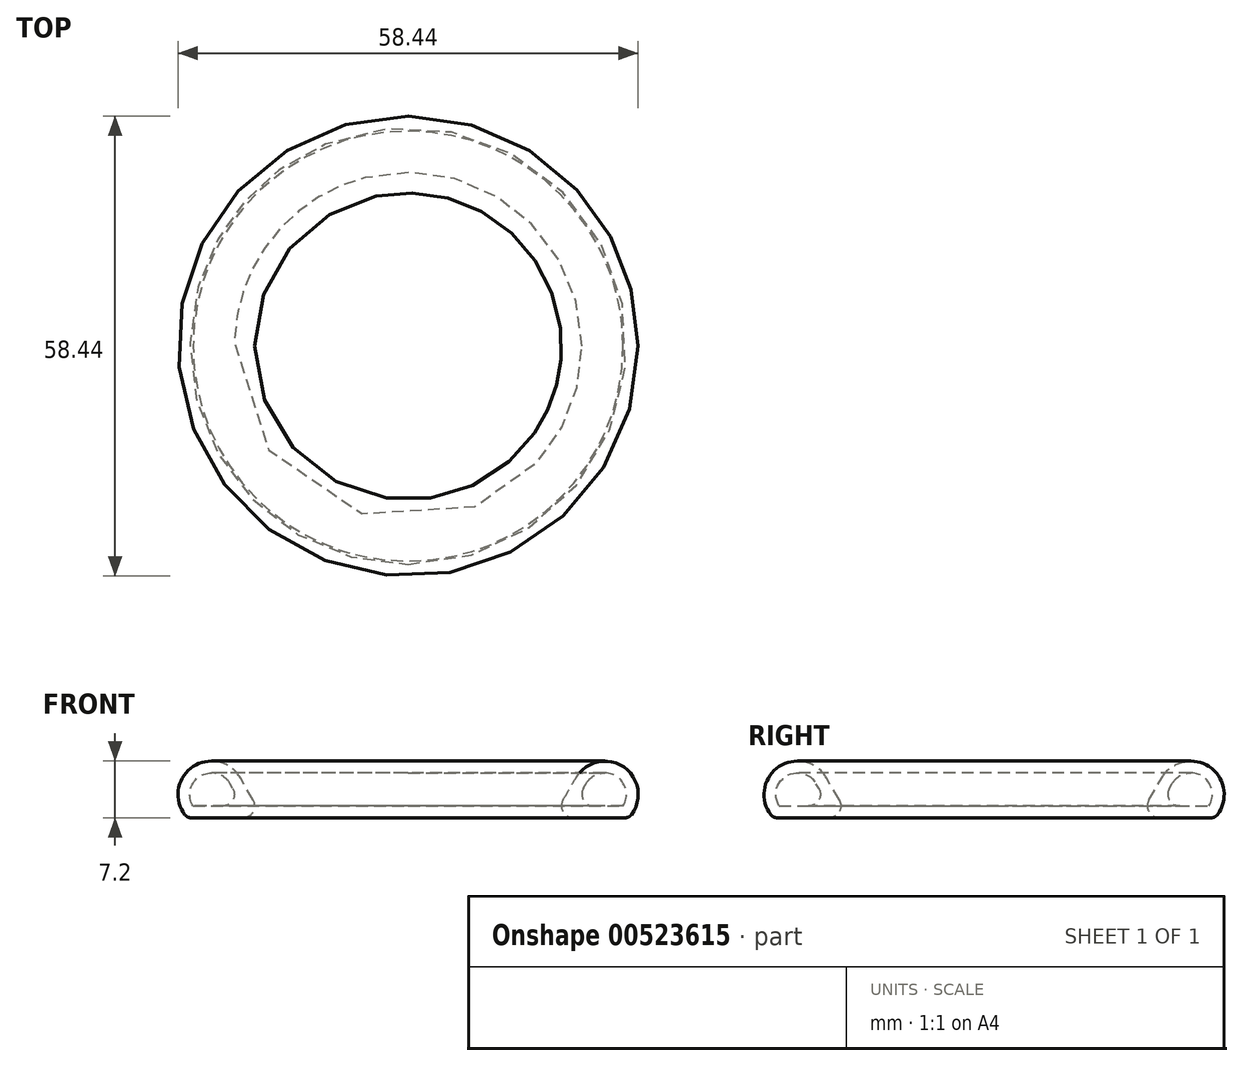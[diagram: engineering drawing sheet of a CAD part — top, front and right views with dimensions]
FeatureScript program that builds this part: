
annotation { "Feature Type Name" : "Feature", "Feature Type Description" : "" }
export const myFeature = defineFeature(function(context is Context, id is Id, definition is map)
    precondition{}
    {
        {
            var Q0;
            Q0=qCreatedBy(makeId("Top.planeOp"),FACE);
            var sketch = newSketch(context, id + "F0", { "sketchPlane" : qUnion([Q0])});
            skCircle(sketch, "E0", {"center": v(0, 0) * mm, "radius": 18.38 * mm});
            skPoint(sketch, "E1", {"position": v(0, -18.38) * mm});
            skSolve(sketch);
        }
        {
            var Q0;
            Q0=qCreatedBy(makeId("Top.planeOp"),FACE);
            cPlane(context, id + "F1", {"entities" : qUnion([Q0]), "cplaneType" : CPlaneType.OFFSET, "offset" : 34 * mm, "width" : 152.4 * mm, "height" : 152.4 * mm});
        }
        {
            var Q0;
            Q0=qCreatedBy(makeId("Right.planeOp"),FACE);
            var sketch = newSketch(context, id + "F2", { "sketchPlane" : qUnion([Q0])});
            skLineSegment(sketch, "E2", {"start": v(-21.3, 5.08) * mm, "end": v(-18.37, 0) * mm});
            skArc(sketch, "E3", {"start": v(-21.3, 5.08) * mm, "mid": v(-27.54, 6.34) * mm, "end": v(-28.03, 0) * mm});
            skLineSegment(sketch, "E4", {"start": v(-28.03, 0) * mm, "end": v(-18.38, 0) * mm});
            skLineSegment(sketch, "E5.0", {"start": v(-27.3, 1.5) * mm, "end": v(-20.97, 1.5) * mm});
            skArc(sketch, "E5.1", {"start": v(-22.6, 4.33) * mm, "mid": v(-26.4, 5.3) * mm, "end": v(-27.3, 1.5) * mm});
            skLineSegment(sketch, "E5.2", {"start": v(-22.6, 4.33) * mm, "end": v(-20.97, 1.5) * mm});
            skSolve(sketch);
        }
        {
            var Q0;
            Q0 = qSketchRegion(id + "F2", true);
            var Q1;
            Q1=sQuery(id+"F0.wireOp",EDGE,"E0");
            sweep(context, id + "F3", {"profiles" : qUnion([Q0]), "path" : qUnion([Q1])});
        }
        {
            var Q0;
            Q0=makeQuery(id+"F3.opSweep","SWEPT_EDGE",EDGE,{"disambiguationData":[OSD([sQuery(id+"F0.wireOp",EDGE,"E0"),sQuery(id+"F2.wireOp",EDGE,"E5.0"),sQuery(id+"F2.wireOp",EDGE,"E5.2")])]});
            fillet(context, id + "F4", {"entities" : qUnion([Q0]), "radius" : 1.5 * mm, "tangentPropagation" : true, "allowEdgeOverflow" : false});
        }
        {
            var Q0;
            Q0=makeQuery(id+"F3.opSweep","SWEPT_EDGE",EDGE,{"disambiguationData":[OSD([sQuery(id+"F0.wireOp",EDGE,"E0"),sQuery(id+"F2.wireOp",EDGE,"E3"),sQuery(id+"F2.wireOp",EDGE,"E4")])]});
            fillet(context, id + "F5", {"entities" : qUnion([Q0]), "radius" : 1 * mm, "tangentPropagation" : true, "allowEdgeOverflow" : false});
        }
        {
            var Q0;
            Q0=makeQuery(id+"F3.opSweep","SWEPT_EDGE",EDGE,{"disambiguationData":[OSD([sQuery(id+"F0.wireOp",EDGE,"E0"),sQuery(id+"F2.wireOp",EDGE,"E2"),sQuery(id+"F2.wireOp",EDGE,"E4")])]});
            fillet(context, id + "F6", {"entities" : qUnion([Q0]), "radius" : 1.5 * mm, "tangentPropagation" : true, "allowEdgeOverflow" : false});
        }
    });
